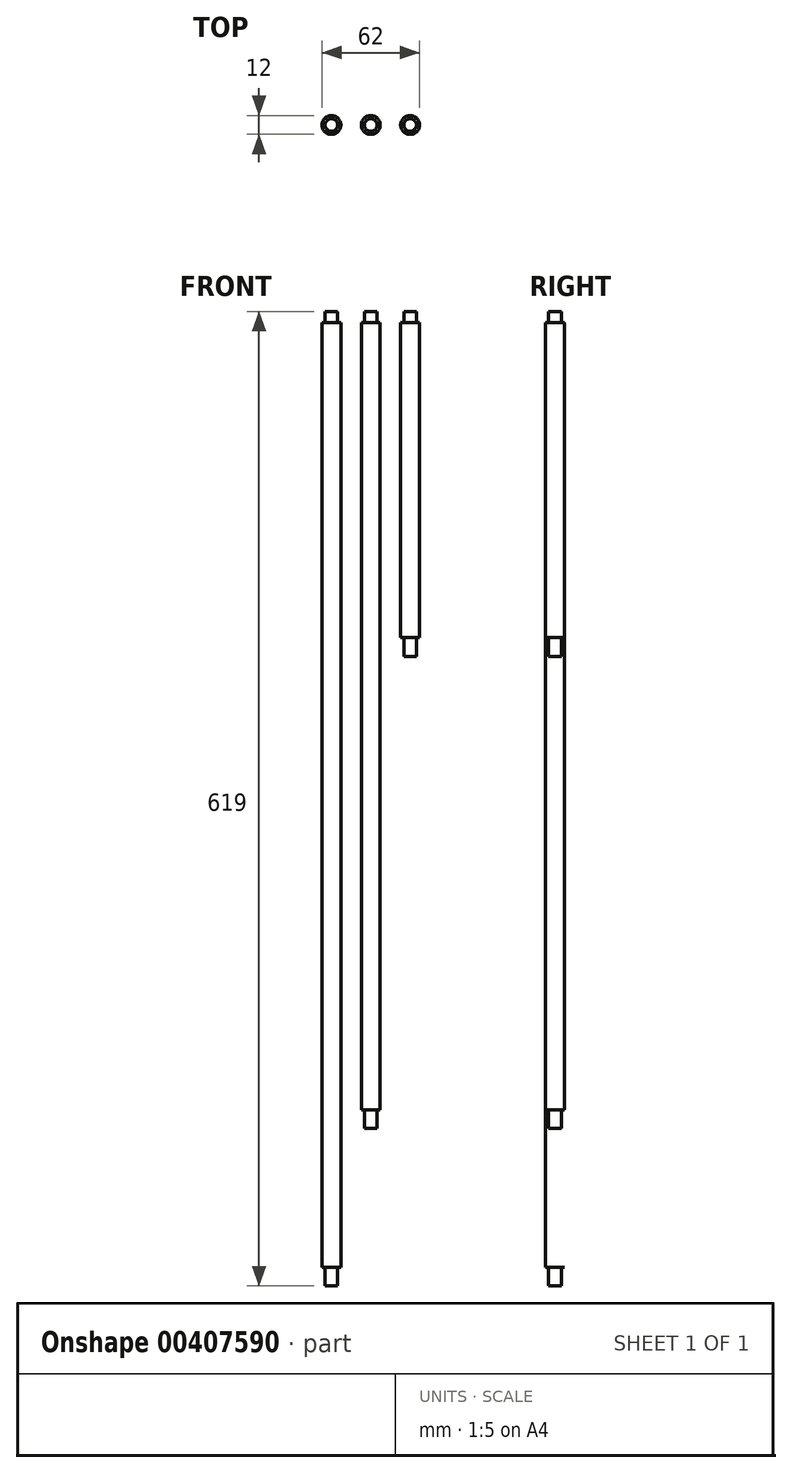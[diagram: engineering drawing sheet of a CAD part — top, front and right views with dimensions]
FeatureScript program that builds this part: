
annotation { "Feature Type Name" : "Feature", "Feature Type Description" : "" }
export const myFeature = defineFeature(function(context is Context, id is Id, definition is map)
    precondition{}
    {
        {
            assignVariable(context, id + "F0", {"name" : "xg", "anyValue" : 500});
        }
        {
            assignVariable(context, id + "F1", {"name" : "yg", "anyValue" : 600});
        }
        {
            assignVariable(context, id + "F2", {"name" : "zg", "anyValue" : 200});
        }
        {
            assignVariable(context, id + "F3", {"name" : "ms", "anyValue" : 7});
        }
        {
            assignVariable(context, id + "F4", {"name" : "bs", "anyValue" : 12});
        }
        {
            var Q0;
            Q0=qCreatedBy(makeId("Top.planeOp"),FACE);
            var sketch = newSketch(context, id + "F5", { "sketchPlane" : qUnion([Q0])});
            skLineSegment(sketch, "E0", {"start": v(-25, 0) * mm, "end": v(25, 0) * mm, "construction": true});
            skCircle(sketch, "E1", {"center": v(-25, 0) * mm, "radius": 6 * mm});
            skCircle(sketch, "E2", {"center": v(0, 0) * mm, "radius": 6 * mm});
            skCircle(sketch, "E3", {"center": v(25, 0) * mm, "radius": 6 * mm});
            skCircle(sketch, "E4", {"center": v(-25, 0) * mm, "radius": 4 * mm});
            skCircle(sketch, "E5", {"center": v(25, 0) * mm, "radius": 4 * mm});
            skCircle(sketch, "E6", {"center": v(0, 0) * mm, "radius": 4 * mm});
            skSolve(sketch);
        }
        {
            var Q0;
            Q0=makeQuery(id+"F5.imprint","IMPRINT",FACE,{"disambiguationData":[TD([[makeQuery(id+"F5.imprint","IMPRINT",EDGE,{"derivedFrom":sQuery(id+"F5.wireOp",EDGE,"E1")}),1.0]])]});
            var Q1;
            Q1=makeQuery(id+"F5.imprint","IMPRINT",FACE,{"disambiguationData":[TD([[makeQuery(id+"F5.imprint","IMPRINT",EDGE,{"derivedFrom":sQuery(id+"F5.wireOp",EDGE,"E4")}),1.0]])]});
            extrude(context, id + "F6", {"entities" : qUnion([Q0, Q1]), "oppositeDirection" : true, "depth" : (getVariable(context, 'yg')) * mm});
        }
        {
            var Q0;
            Q0=makeQuery(id+"F5.imprint","IMPRINT",FACE,{"disambiguationData":[TD([[makeQuery(id+"F5.imprint","IMPRINT",EDGE,{"derivedFrom":sQuery(id+"F5.wireOp",EDGE,"E2")}),1.0]])]});
            var Q1;
            Q1=makeQuery(id+"F5.imprint","IMPRINT",FACE,{"disambiguationData":[TD([[makeQuery(id+"F5.imprint","IMPRINT",EDGE,{"derivedFrom":sQuery(id+"F5.wireOp",EDGE,"E6")}),1.0]])]});
            extrude(context, id + "F7", {"entities" : qUnion([Q0, Q1]), "oppositeDirection" : true, "depth" : (getVariable(context, 'xg')) * mm});
        }
        {
            var Q0;
            Q0=makeQuery(id+"F5.imprint","IMPRINT",FACE,{"disambiguationData":[TD([[makeQuery(id+"F5.imprint","IMPRINT",EDGE,{"derivedFrom":sQuery(id+"F5.wireOp",EDGE,"E3")}),1.0]])]});
            var Q1;
            Q1=makeQuery(id+"F5.imprint","IMPRINT",FACE,{"disambiguationData":[TD([[makeQuery(id+"F5.imprint","IMPRINT",EDGE,{"derivedFrom":sQuery(id+"F5.wireOp",EDGE,"E5")}),1.0]])]});
            extrude(context, id + "F8", {"entities" : qUnion([Q0, Q1]), "oppositeDirection" : true, "depth" : (getVariable(context, 'zg')) * mm});
        }
        {
            var Q0;
            Q0=makeQuery(id+"F5.imprint","IMPRINT",FACE,{"disambiguationData":[TD([[makeQuery(id+"F5.imprint","IMPRINT",EDGE,{"derivedFrom":sQuery(id+"F5.wireOp",EDGE,"E4")}),1.0]])]});
            var Q1;
            Q1=makeQuery(id+"F5.imprint","IMPRINT",FACE,{"disambiguationData":[TD([[makeQuery(id+"F5.imprint","IMPRINT",EDGE,{"derivedFrom":sQuery(id+"F5.wireOp",EDGE,"E6")}),1.0]])]});
            var Q2;
            Q2=makeQuery(id+"F5.imprint","IMPRINT",FACE,{"disambiguationData":[TD([[makeQuery(id+"F5.imprint","IMPRINT",EDGE,{"derivedFrom":sQuery(id+"F5.wireOp",EDGE,"E5")}),1.0]])]});
            extrude(context, id + "F9", {"entities" : qUnion([Q0, Q1, Q2]), "operationType" : NewBodyOperationType.ADD, "depth" : (getVariable(context, 'ms')) * mm});
        }
        {
            var Q0;
            Q0=makeQuery(id+"F5.imprint","IMPRINT",FACE,{"disambiguationData":[TD([[makeQuery(id+"F5.imprint","IMPRINT",EDGE,{"derivedFrom":sQuery(id+"F5.wireOp",EDGE,"E5")}),1.0]])]});
            var Q1;
            Q1=makeQuery(id+"F5.imprint","IMPRINT",FACE,{"disambiguationData":[TD([[makeQuery(id+"F5.imprint","IMPRINT",EDGE,{"derivedFrom":sQuery(id+"F5.wireOp",EDGE,"E6")}),1.0]])]});
            var Q2;
            Q2=makeQuery(id+"F5.imprint","IMPRINT",FACE,{"disambiguationData":[TD([[makeQuery(id+"F5.imprint","IMPRINT",EDGE,{"derivedFrom":sQuery(id+"F5.wireOp",EDGE,"E4")}),1.0]])]});
            var Q3;
            Q3=makeQuery(id+"F6.opExtrude","CAP_FACE",FACE,{"disambiguationData":[OSD([sQuery(id+"F5.wireOp",EDGE,"E1")])],"isStart":false});
            var Q4;
            Q4=makeQuery(id+"F8.opExtrude","CAP_FACE",FACE,{"disambiguationData":[OSD([sQuery(id+"F5.wireOp",EDGE,"E3")])],"isStart":false});
            extrude(context, id + "F10", {"entities" : qUnion([Q0, Q1, Q2]), "operationType" : NewBodyOperationType.ADD, "oppositeDirection" : true, "endBoundEntityFace" : qUnion([Q3]), "depth" : (getVariable(context, 'zg') + getVariable(context, 'bs')) * mm, "hasSecondDirection" : true, "secondDirectionBound" : BoundingType.UP_TO_SURFACE, "secondDirectionOppositeDirection" : true, "secondDirectionBoundEntityFace" : qUnion([Q4]), "secondDirectionDepth" : 206.2 * mm});
        }
        {
            var Q0;
            Q0=makeQuery(id+"F5.imprint","IMPRINT",FACE,{"disambiguationData":[TD([[makeQuery(id+"F5.imprint","IMPRINT",EDGE,{"derivedFrom":sQuery(id+"F5.wireOp",EDGE,"E6")}),1.0]])]});
            var Q1;
            Q1=makeQuery(id+"F7.opExtrude","CAP_FACE",FACE,{"disambiguationData":[OSD([sQuery(id+"F5.wireOp",EDGE,"E2")])],"isStart":false});
            extrude(context, id + "F11", {"entities" : qUnion([Q0]), "operationType" : NewBodyOperationType.ADD, "oppositeDirection" : true, "depth" : (getVariable(context, 'xg') + getVariable(context, 'bs')) * mm, "hasSecondDirection" : true, "secondDirectionBound" : BoundingType.UP_TO_SURFACE, "secondDirectionOppositeDirection" : true, "secondDirectionBoundEntityFace" : qUnion([Q1]), "secondDirectionDepth" : 537 * mm});
        }
        {
            var Q0;
            Q0=makeQuery(id+"F5.imprint","IMPRINT",FACE,{"disambiguationData":[TD([[makeQuery(id+"F5.imprint","IMPRINT",EDGE,{"derivedFrom":sQuery(id+"F5.wireOp",EDGE,"E4")}),1.0]])]});
            var Q1;
            Q1=makeQuery(id+"F6.opExtrude","CAP_FACE",FACE,{"disambiguationData":[OSD([sQuery(id+"F5.wireOp",EDGE,"E1")])],"isStart":false});
            extrude(context, id + "F12", {"entities" : qUnion([Q0]), "operationType" : NewBodyOperationType.ADD, "oppositeDirection" : true, "depth" : (getVariable(context, 'yg') + getVariable(context, 'bs')) * mm, "hasSecondDirection" : true, "secondDirectionBound" : BoundingType.UP_TO_SURFACE, "secondDirectionOppositeDirection" : true, "secondDirectionBoundEntityFace" : qUnion([Q1]), "secondDirectionDepth" : 648 * mm});
        }
    });
